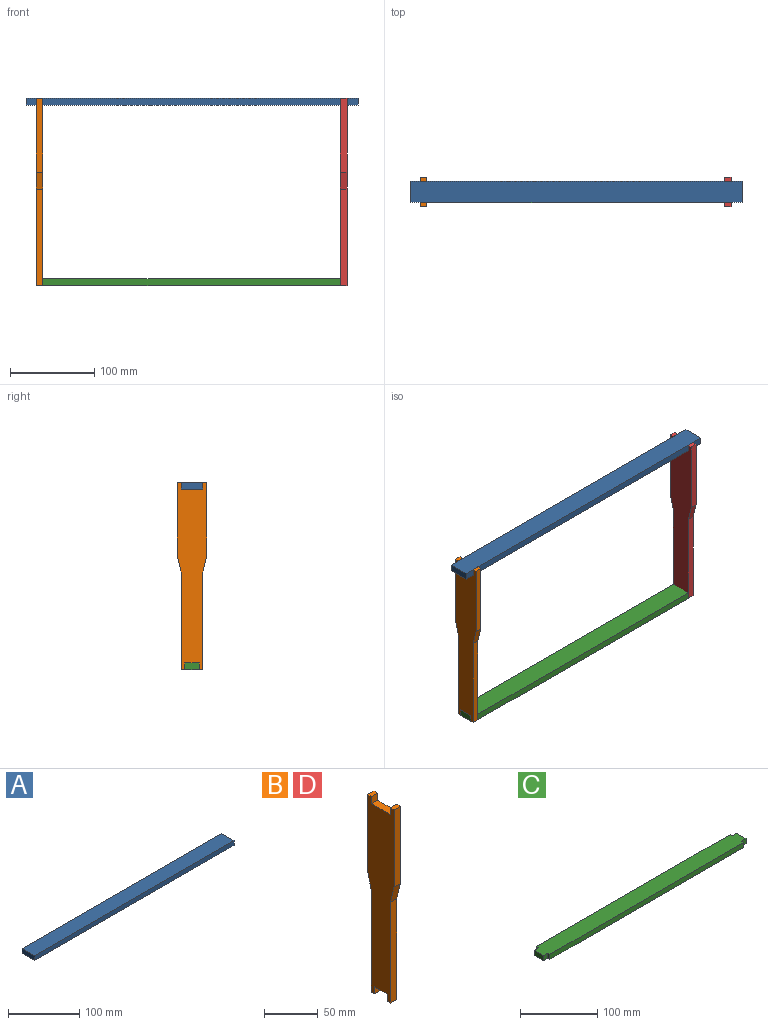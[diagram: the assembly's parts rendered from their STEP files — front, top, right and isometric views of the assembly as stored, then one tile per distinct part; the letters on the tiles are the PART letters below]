
ASSEMBLY  parts=4 mates=3
PART A: 6 faces, bbox 395x25x8 mm
  f0: plane 395x25mm, normal (0,0,1), area 9875mm2, adj f1,f3,f4,f5
  f1: plane 395x8mm, normal (0,-1,0), area 3160mm2, adj f0,f2,f4,f5
  f2: plane 395x25mm, normal (0,0,-1), area 9875mm2, adj f1,f3,f4,f5
  f3: plane 395x8mm, normal (0,1,0), area 3160mm2, adj f0,f2,f4,f5
  f4: plane 25x8mm, normal (1,0,0), area 200mm2, adj f0,f1,f2,f3
  f5: plane 25x8mm, normal (-1,0,0), area 200mm2, adj f0,f1,f2,f3
PART B: 18 faces, bbox 8x35x223 mm
  f0: plane 88x8mm, normal (0,1,0), area 704mm2, adj f1,f15,f16,f17
  f1: plane 8x5mm, normal (0,0,1), area 40mm2, adj f0,f2,f16,f17
  f2: plane 8x8mm, normal (0,-1,0), area 64mm2, adj f1,f3,f16,f17
  f3: plane 25x8mm, normal (0,0,1), area 200mm2, adj f2,f4,f16,f17
  f4: plane 8x8mm, normal (0,1,0), area 64mm2, adj f3,f5,f16,f17
  f5: plane 8x5mm, normal (0,0,1), area 40mm2, adj f4,f6,f16,f17
  f6: plane 88x8mm, normal (0,-1,0), area 704mm2, adj f5,f7,f16,f17
  f7: plane 20x8mm, normal (0,-0.97,-0.24), area 164.9mm2, adj f6,f8,f16,f17
  f8: plane 115x8mm, normal (0,-1,0), area 920mm2, adj f7,f9,f16,f17
  f9: plane 8x4mm, normal (0,0,-1), area 32mm2, adj f8,f10,f16,f17
  f10: plane 8x8mm, normal (0,1,0), area 64mm2, adj f9,f11,f16,f17
  f11: plane 17x8mm, normal (0,0,-1), area 136mm2, adj f10,f12,f16,f17
  f12: plane 8x8mm, normal (0,-1,0), area 64mm2, adj f11,f13,f16,f17
  f13: plane 8x4mm, normal (0,0,-1), area 32mm2, adj f12,f14,f16,f17
  f14: plane 115x8mm, normal (0,1,0), area 920mm2, adj f13,f15,f16,f17
  f15: plane 20x8mm, normal (0,0.97,-0.24), area 164.9mm2, adj f0,f14,f16,f17
  f16: plane 223x35mm, normal (1,0,0), area 6219mm2, adj f0,f1,f2,f3,f4,f5,f6,f7
  f17: plane 223x35mm, normal (-1,0,0), area 6219mm2, adj f0,f1,f2,f3,f4,f5,f6,f7
PART C: 14 faces, bbox 370x25x8 mm
  f0: plane 370x25mm, normal (0,0,1), area 9122mm2, adj f1,f2,f3,f4,f6,f7,f8,f9
  f1: plane 354x8mm, normal (0,-1,0), area 2832mm2, adj f0,f5,f7,f13
  f2: plane 354x8mm, normal (0,1,0), area 2832mm2, adj f0,f5,f9,f11
  f3: plane 17x8mm, normal (1,0,0), area 136mm2, adj f0,f5,f6,f8
  f4: plane 17x8mm, normal (-1,0,0), area 136mm2, adj f0,f5,f10,f12
  f5: plane 370x25mm, normal (0,0,-1), area 9122mm2, adj f1,f2,f3,f4,f6,f7,f8,f9
  f6: plane 8x8mm, normal (0,-1,0), area 64mm2, adj f0,f3,f5,f7
  f7: plane 8x4mm, normal (1,0,0), area 32mm2, adj f0,f1,f5,f6
  f8: plane 8x8mm, normal (0,1,0), area 64mm2, adj f0,f3,f5,f9
  f9: plane 8x4mm, normal (1,0,0), area 32mm2, adj f0,f2,f5,f8
  f10: plane 8x8mm, normal (0,1,0), area 64mm2, adj f0,f4,f5,f11
  f11: plane 8x4mm, normal (-1,0,0), area 32mm2, adj f0,f2,f5,f10
  f12: plane 8x8mm, normal (0,-1,0), area 64mm2, adj f0,f4,f5,f13
  f13: plane 8x4mm, normal (-1,0,0), area 32mm2, adj f0,f1,f5,f12
PART D: same geometry as B
PLACE A t=(12.49,71.2,182.06)mm
PLACE B t=(24.49,71.2,-36.94)mm
PLACE C t=(24.49,71.2,-32.94)mm
PLACE D t=(386.49,71.2,-36.94)mm
MATE fastened B.f3 <-> A.f2  axis (0,0,1) through (24.49,71.2,178.06)mm
MATE fastened C.f0 <-> D.f11  axis (0,0,1) through (394.49,71.2,-28.94)mm
MATE fastened B.f11 <-> C.f0  axis (0,0,-1) through (24.49,71.2,-28.94)mm
